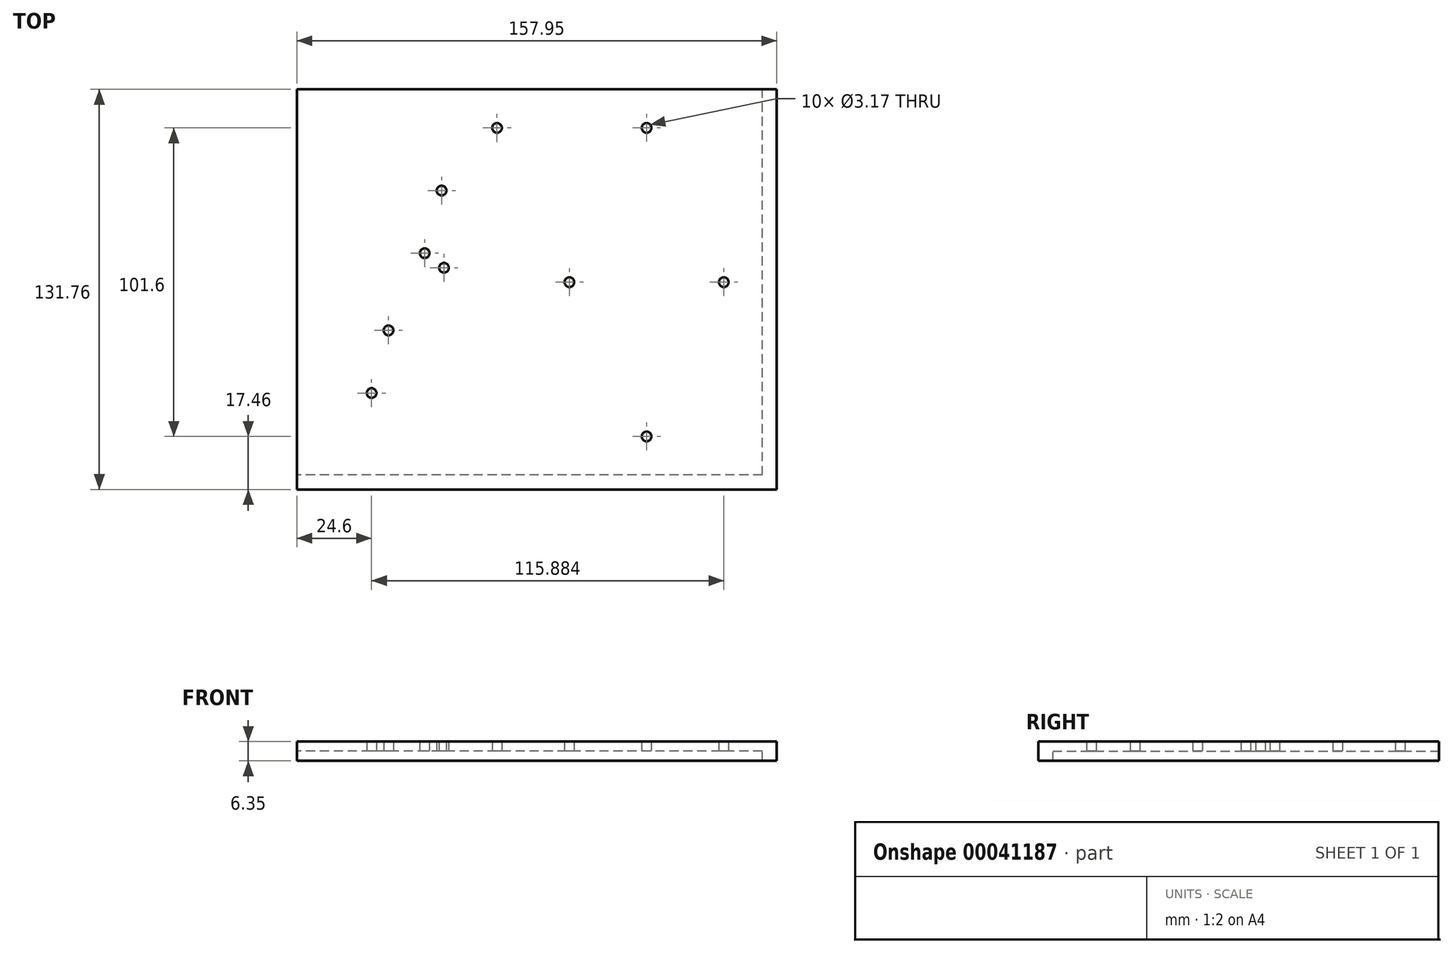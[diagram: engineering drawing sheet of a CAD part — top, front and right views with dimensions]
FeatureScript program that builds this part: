
annotation { "Feature Type Name" : "Feature", "Feature Type Description" : "" }
export const myFeature = defineFeature(function(context is Context, id is Id, definition is map)
    precondition{}
    {
        {
            var Q0;
            Q0=qCreatedBy(makeId("Top.planeOp"),FACE);
            var sketch = newSketch(context, id + "F0", { "sketchPlane" : qUnion([Q0])});
            skLineSegment(sketch, "E0.rect.bottom", {"start": v(76.6, -63.5) * mm, "end": v(-76.6, -63.5) * mm});
            skLineSegment(sketch, "E0.rect.top", {"start": v(76.6, 63.5) * mm, "end": v(-76.6, 63.5) * mm});
            skLineSegment(sketch, "E0.rect.left", {"start": v(76.6, -63.5) * mm, "end": v(76.6, 63.5) * mm});
            skLineSegment(sketch, "E0.rect.right", {"start": v(-76.6, -63.5) * mm, "end": v(-76.6, 63.5) * mm});
            skPoint(sketch, "E0.rect.middle", {"position": v(0, 0) * mm});
            skCircle(sketch, "E1", {"center": v(38.5, 50.8) * mm, "radius": 1.59 * mm});
            skCircle(sketch, "E2", {"center": v(38.5, -50.8) * mm, "radius": 1.59 * mm});
            skPoint(sketch, "E3", {"position": v(38.5, 0) * mm});
            skCircle(sketch, "E4", {"center": v(13.1, 0) * mm, "radius": 1.59 * mm});
            skCircle(sketch, "E5", {"center": v(63.9, 0) * mm, "radius": 1.59 * mm});
            skLineSegment(sketch, "E6", {"start": v(-76.6, -68.26) * mm, "end": v(81.36, -68.26) * mm});
            skLineSegment(sketch, "E7", {"start": v(81.36, -68.26) * mm, "end": v(81.36, 63.5) * mm});
            skLineSegment(sketch, "E8", {"start": v(81.36, 63.5) * mm, "end": v(76.6, 63.5) * mm});
            skPoint(sketch, "E9.center.orphan", {"position": v(-22.62, -28.57) * mm});
            skPoint(sketch, "E10.center.orphan", {"position": v(-22.62, 28.58) * mm});
            skPoint(sketch, "E11.center.orphan", {"position": v(-41.67, 28.58) * mm});
            skPoint(sketch, "E12.center.orphan", {"position": v(-41.67, -28.57) * mm});
            skPoint(sketch, "E13", {"position": v(-10.7, 4.75) * mm});
            skCircle(sketch, "E14", {"center": v(-28.17, 4.75) * mm, "radius": 1.59 * mm});
            skPoint(sketch, "E15", {"position": v(-34.53, -36.5) * mm});
            skPoint(sketch, "E16", {"position": v(-28.97, -15.87) * mm});
            skCircle(sketch, "E17", {"center": v(-51.99, -36.5) * mm, "radius": 1.59 * mm});
            skCircle(sketch, "E18", {"center": v(-46.43, -15.87) * mm, "radius": 1.59 * mm});
            skPoint(sketch, "E19.center.orphan", {"position": v(-28.97, -28.57) * mm});
            skPoint(sketch, "E20.center.orphan", {"position": v(-10.7, -7.95) * mm});
            skPoint(sketch, "E21.center.orphan", {"position": v(-34.53, -49.2) * mm});
            skPoint(sketch, "E22.center.orphan", {"position": v(-10.7, 49.2) * mm});
            skCircle(sketch, "E23", {"center": v(-10.7, 50.79) * mm, "radius": 1.59 * mm});
            skPoint(sketch, "E24.center.orphan", {"position": v(-28.97, 28.58) * mm});
            skCircle(sketch, "E25", {"center": v(-28.97, 30.16) * mm, "radius": 1.59 * mm});
            skPoint(sketch, "E26.center.orphan", {"position": v(-34.53, 7.95) * mm});
            skCircle(sketch, "E27", {"center": v(-34.53, 9.54) * mm, "radius": 1.59 * mm});
            skLineSegment(sketch, "E28", {"start": v(-76.6, -63.5) * mm, "end": v(-76.6, -68.26) * mm});
            skPoint(sketch, "E29.end.orphan", {"position": v(-81.36, -68.26) * mm});
            skSolve(sketch);
        }
        {
            var Q0;
            Q0=makeQuery(id+"F0.imprint","IMPRINT",FACE,{"disambiguationData":[TD([[makeQuery(id+"F0.imprint","IMPRINT",EDGE,{"derivedFrom":sQuery(id+"F0.wireOp",EDGE,"E0.rect.bottom")}),1.0]])]});
            var Q1;
            Q1=makeQuery(id+"F0.imprint","IMPRINT",FACE,{"disambiguationData":[TD([[makeQuery(id+"F0.imprint","IMPRINT",EDGE,{"derivedFrom":sQuery(id+"F0.wireOp",EDGE,"E0.rect.bottom")}),-1.0]])]});
            extrude(context, id + "F1", {"entities" : qUnion([Q0, Q1]), "depth" : 3.17 * mm});
        }
        {
            var Q0;
            Q0=makeQuery(id+"F0.imprint","IMPRINT",FACE,{"disambiguationData":[TD([[makeQuery(id+"F0.imprint","IMPRINT",EDGE,{"derivedFrom":sQuery(id+"F0.wireOp",EDGE,"E0.rect.bottom")}),1.0]])]});
            extrude(context, id + "F2", {"entities" : qUnion([Q0]), "operationType" : NewBodyOperationType.ADD, "oppositeDirection" : true, "depth" : 3.17 * mm});
        }
    });
